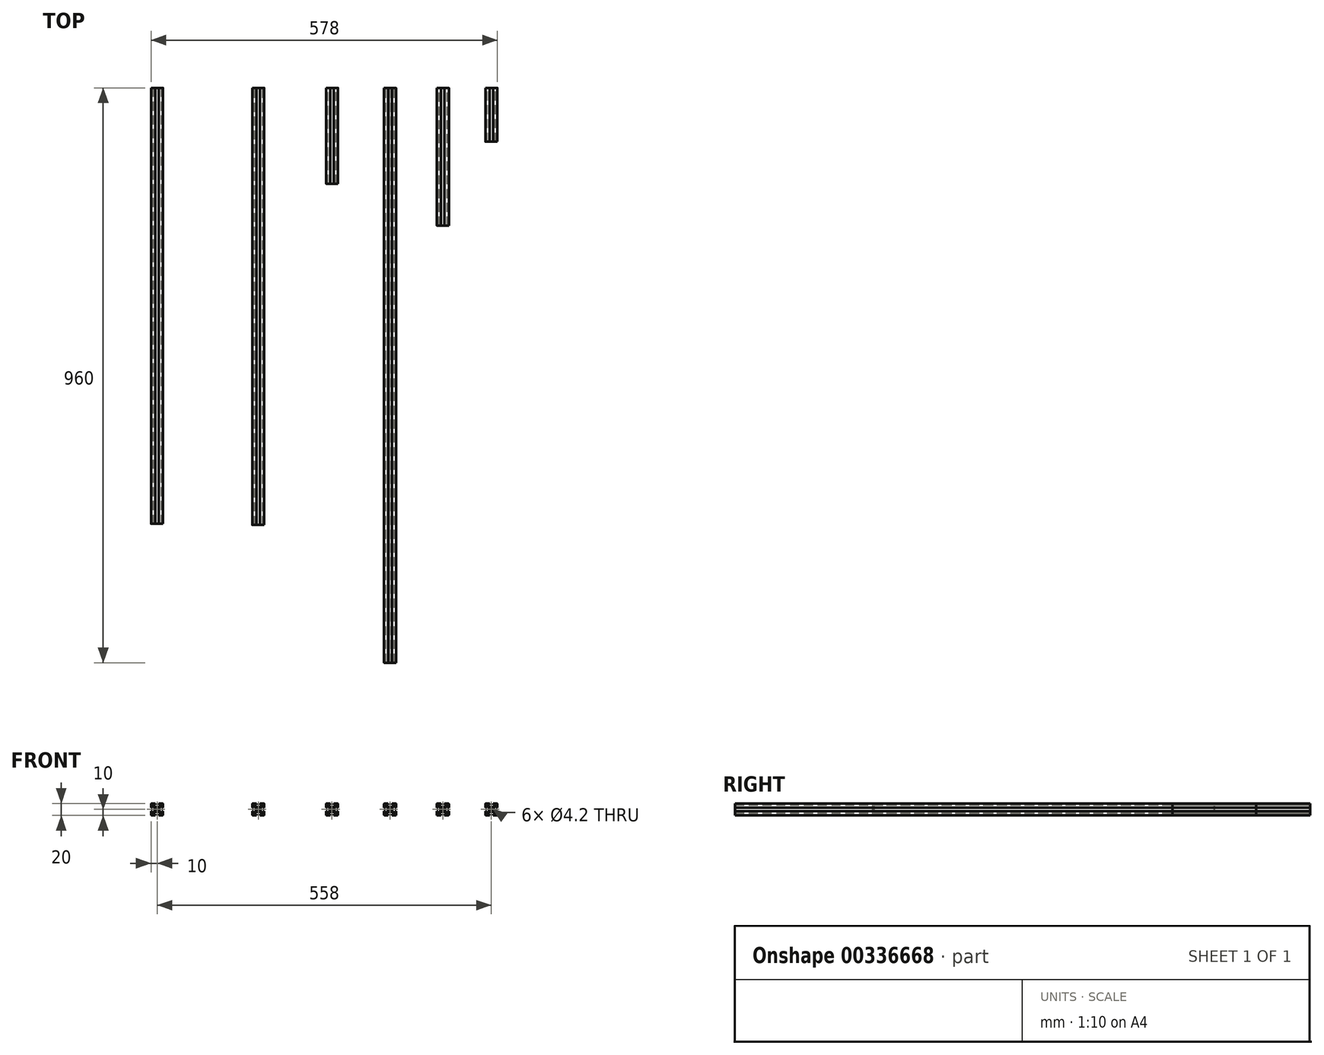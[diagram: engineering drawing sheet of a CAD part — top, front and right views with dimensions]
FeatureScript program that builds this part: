
annotation { "Feature Type Name" : "Feature", "Feature Type Description" : "" }
export const myFeature = defineFeature(function(context is Context, id is Id, definition is map)
    precondition{}
    {
        {
            var Q0;
            Q0=qCreatedBy(makeId("Front.planeOp"),FACE);
            var sketch = newSketch(context, id + "F0", { "sketchPlane" : qUnion([Q0])});
            skCircle(sketch, "E0", {"center": v(0, 0) * mm, "radius": 2.1 * mm});
            skLineSegment(sketch, "E1.bottom", {"start": v(9, 10) * mm, "end": v(3, 10) * mm});
            skLineSegment(sketch, "E1.top", {"start": v(9, -10) * mm, "end": v(3, -10) * mm});
            skLineSegment(sketch, "E1.left", {"start": v(10, 9) * mm, "end": v(10, 3) * mm});
            skLineSegment(sketch, "E1.right", {"start": v(-10, 9) * mm, "end": v(-10, 3) * mm});
            skLineSegment(sketch, "E2.bottom", {"start": v(2.94, 4) * mm, "end": v(-2.94, 4) * mm});
            skLineSegment(sketch, "E2.top", {"start": v(2.94, -4) * mm, "end": v(-2.94, -4) * mm});
            skLineSegment(sketch, "E2.left", {"start": v(4, 2.94) * mm, "end": v(4, -2.94) * mm});
            skLineSegment(sketch, "E2.right", {"start": v(-4, 2.94) * mm, "end": v(-4, -2.94) * mm});
            skLineSegment(sketch, "E3.bottom", {"start": v(6.94, 8) * mm, "end": v(3, 8) * mm});
            skLineSegment(sketch, "E3.top", {"start": v(6.94, -8) * mm, "end": v(3, -8) * mm});
            skLineSegment(sketch, "E3.left", {"start": v(8, 6.94) * mm, "end": v(8, 3) * mm});
            skLineSegment(sketch, "E3.right", {"start": v(-8, 6.94) * mm, "end": v(-8, 3) * mm});
            skLineSegment(sketch, "E4", {"start": v(-3, -10) * mm, "end": v(-3, -8) * mm});
            skLineSegment(sketch, "E5.MirrorCS", {"start": v(3, -10) * mm, "end": v(3, -8) * mm});
            skLineSegment(sketch, "E6.MirrorCS", {"start": v(-3, 10) * mm, "end": v(-3, 8) * mm});
            skLineSegment(sketch, "E7.MirrorCS", {"start": v(3, 10) * mm, "end": v(3, 8) * mm});
            skLineSegment(sketch, "E8", {"start": v(-10, 3) * mm, "end": v(-8, 3) * mm});
            skLineSegment(sketch, "E9.MirrorCS", {"start": v(-10, -3) * mm, "end": v(-8, -3) * mm});
            skLineSegment(sketch, "E10", {"start": v(8, 3) * mm, "end": v(10, 3) * mm});
            skLineSegment(sketch, "E11.MirrorCS", {"start": v(8, -3) * mm, "end": v(10, -3) * mm});
            skPoint(sketch, "E12", {"position": v(-8, -6.94) * mm});
            skPoint(sketch, "E13", {"position": v(6.94, 8) * mm});
            skPoint(sketch, "E14", {"position": v(-4, -2.94) * mm});
            skPoint(sketch, "E15", {"position": v(2.94, 4) * mm});
            skLineSegment(sketch, "E16", {"start": v(-8, -6.94) * mm, "end": v(-4, -2.94) * mm});
            skLineSegment(sketch, "E17", {"start": v(2.94, 4) * mm, "end": v(6.94, 8) * mm});
            skLineSegment(sketch, "E18.MirrorCS", {"start": v(-6.94, -8) * mm, "end": v(-2.94, -4) * mm});
            skLineSegment(sketch, "E19.1.0", {"start": v(6.94, -8) * mm, "end": v(2.94, -4) * mm});
            skLineSegment(sketch, "E19.2.0", {"start": v(8, 6.94) * mm, "end": v(4, 2.94) * mm});
            skLineSegment(sketch, "E19.3.0", {"start": v(-6.94, 8) * mm, "end": v(-2.94, 4) * mm});
            skLineSegment(sketch, "E20.1.0", {"start": v(8, -6.94) * mm, "end": v(4, -2.94) * mm});
            skLineSegment(sketch, "E20.2.0", {"start": v(6.94, 8) * mm, "end": v(2.94, 4) * mm});
            skLineSegment(sketch, "E20.3.0", {"start": v(-8, 6.94) * mm, "end": v(-4, 2.94) * mm});
            skLineSegment(sketch, "E21.trimOffspring", {"start": v(-3, 8) * mm, "end": v(-6.94, 8) * mm});
            skLineSegment(sketch, "E22.trimOffspring", {"start": v(-3, 10) * mm, "end": v(-9, 10) * mm});
            skLineSegment(sketch, "E23.trimOffspring", {"start": v(8, -3) * mm, "end": v(8, -6.94) * mm});
            skLineSegment(sketch, "E24.trimOffspring", {"start": v(10, -3) * mm, "end": v(10, -9) * mm});
            skLineSegment(sketch, "E25.trimOffspring", {"start": v(-3, -10) * mm, "end": v(-9, -10) * mm});
            skLineSegment(sketch, "E26.trimOffspring", {"start": v(-3, -8) * mm, "end": v(-6.94, -8) * mm});
            skLineSegment(sketch, "E27.trimOffspring", {"start": v(-10, -3) * mm, "end": v(-10, -9) * mm});
            skLineSegment(sketch, "E28.trimOffspring", {"start": v(-8, -3) * mm, "end": v(-8, -6.94) * mm});
            skArc(sketch, "E29.filletArc", {"start": v(-10, -9) * mm, "mid": v(-9.7, -9.7) * mm, "end": v(-9, -10) * mm});
            skArc(sketch, "E30.filletArc", {"start": v(9, -10) * mm, "mid": v(9.7, -9.7) * mm, "end": v(10, -9) * mm});
            skArc(sketch, "E31.filletArc", {"start": v(10, 9) * mm, "mid": v(9.7, 9.7) * mm, "end": v(9, 10) * mm});
            skArc(sketch, "E32.filletArc", {"start": v(-9, 10) * mm, "mid": v(-9.7, 9.7) * mm, "end": v(-10, 9) * mm});
            skSolve(sketch);
        }
        {
            var Q0;
            Q0=makeQuery(id+"F0.imprint","IMPRINT",FACE,{"disambiguationData":[TD([[makeQuery(id+"F0.imprint","IMPRINT",EDGE,{"derivedFrom":sQuery(id+"F0.wireOp",EDGE,"E0")}),-1.0]])]});
            extrude(context, id + "F1", {"entities" : qUnion([Q0]), "depth" : 960 * mm});
        }
        {
            var Q0;
            Q0 = qSketchRegion(id + "F0", true);
            extrude(context, id + "F2", {"entities" : qUnion([Q0]), "depth" : 230 * mm});
        }
        {
            var Q0;
            Q0=makeQuery(id+"F2.opExtrude","SWEPT_BODY",BODY,{"disambiguationData":[OSD([sQuery(id+"F0.wireOp",EDGE,"E0"),sQuery(id+"F0.wireOp",EDGE,"E1.bottom"),sQuery(id+"F0.wireOp",EDGE,"E1.top"),sQuery(id+"F0.wireOp",EDGE,"E1.left"),sQuery(id+"F0.wireOp",EDGE,"E1.right"),sQuery(id+"F0.wireOp",EDGE,"E2.bottom"),sQuery(id+"F0.wireOp",EDGE,"E2.top"),sQuery(id+"F0.wireOp",EDGE,"E2.left"),sQuery(id+"F0.wireOp",EDGE,"E2.right"),sQuery(id+"F0.wireOp",EDGE,"E3.bottom"),sQuery(id+"F0.wireOp",EDGE,"E3.top"),sQuery(id+"F0.wireOp",EDGE,"E3.left"),sQuery(id+"F0.wireOp",EDGE,"E3.right"),sQuery(id+"F0.wireOp",EDGE,"E4"),sQuery(id+"F0.wireOp",EDGE,"E5.MirrorCS"),sQuery(id+"F0.wireOp",EDGE,"E6.MirrorCS"),sQuery(id+"F0.wireOp",EDGE,"E7.MirrorCS"),sQuery(id+"F0.wireOp",EDGE,"E8"),sQuery(id+"F0.wireOp",EDGE,"E9.MirrorCS"),sQuery(id+"F0.wireOp",EDGE,"E10"),sQuery(id+"F0.wireOp",EDGE,"E11.MirrorCS"),sQuery(id+"F0.wireOp",EDGE,"E16"),sQuery(id+"F0.wireOp",EDGE,"E18.MirrorCS"),sQuery(id+"F0.wireOp",EDGE,"E19.1.0"),sQuery(id+"F0.wireOp",EDGE,"E19.2.0"),sQuery(id+"F0.wireOp",EDGE,"E19.3.0"),sQuery(id+"F0.wireOp",EDGE,"E20.1.0"),sQuery(id+"F0.wireOp",EDGE,"E20.2.0"),sQuery(id+"F0.wireOp",EDGE,"E20.3.0"),sQuery(id+"F0.wireOp",EDGE,"E21.trimOffspring"),sQuery(id+"F0.wireOp",EDGE,"E22.trimOffspring"),sQuery(id+"F0.wireOp",EDGE,"E23.trimOffspring"),sQuery(id+"F0.wireOp",EDGE,"E24.trimOffspring"),sQuery(id+"F0.wireOp",EDGE,"E25.trimOffspring"),sQuery(id+"F0.wireOp",EDGE,"E26.trimOffspring"),sQuery(id+"F0.wireOp",EDGE,"E27.trimOffspring"),sQuery(id+"F0.wireOp",EDGE,"E28.trimOffspring"),sQuery(id+"F0.wireOp",EDGE,"E29.filletArc"),sQuery(id+"F0.wireOp",EDGE,"E30.filletArc"),sQuery(id+"F0.wireOp",EDGE,"E31.filletArc"),sQuery(id+"F0.wireOp",EDGE,"E32.filletArc")])]});
            transform(context, id + "F3", {"entities" : qUnion([Q0]), "transformType" : TransformType.TRANSLATION_3D, "dx" : 88 * mm, "dy" : 0 * mm, "dz" : 0 * mm, "makeCopy" : false});
        }
        {
            var Q0;
            Q0 = qSketchRegion(id + "F0", true);
            extrude(context, id + "F4", {"entities" : qUnion([Q0]), "depth" : 160 * mm});
        }
        {
            var Q0;
            Q0 = qSketchRegion(id + "F0", true);
            extrude(context, id + "F5", {"entities" : qUnion([Q0]), "depth" : 90 * mm});
        }
        {
            var Q0;
            Q0=makeQuery(id+"F5.opExtrude","SWEPT_BODY",BODY,{"disambiguationData":[OSD([sQuery(id+"F0.wireOp",EDGE,"E0"),sQuery(id+"F0.wireOp",EDGE,"E1.bottom"),sQuery(id+"F0.wireOp",EDGE,"E1.top"),sQuery(id+"F0.wireOp",EDGE,"E1.left"),sQuery(id+"F0.wireOp",EDGE,"E1.right"),sQuery(id+"F0.wireOp",EDGE,"E2.bottom"),sQuery(id+"F0.wireOp",EDGE,"E2.top"),sQuery(id+"F0.wireOp",EDGE,"E2.left"),sQuery(id+"F0.wireOp",EDGE,"E2.right"),sQuery(id+"F0.wireOp",EDGE,"E3.bottom"),sQuery(id+"F0.wireOp",EDGE,"E3.top"),sQuery(id+"F0.wireOp",EDGE,"E3.left"),sQuery(id+"F0.wireOp",EDGE,"E3.right"),sQuery(id+"F0.wireOp",EDGE,"E4"),sQuery(id+"F0.wireOp",EDGE,"E5.MirrorCS"),sQuery(id+"F0.wireOp",EDGE,"E6.MirrorCS"),sQuery(id+"F0.wireOp",EDGE,"E7.MirrorCS"),sQuery(id+"F0.wireOp",EDGE,"E8"),sQuery(id+"F0.wireOp",EDGE,"E9.MirrorCS"),sQuery(id+"F0.wireOp",EDGE,"E10"),sQuery(id+"F0.wireOp",EDGE,"E11.MirrorCS"),sQuery(id+"F0.wireOp",EDGE,"E16"),sQuery(id+"F0.wireOp",EDGE,"E18.MirrorCS"),sQuery(id+"F0.wireOp",EDGE,"E19.1.0"),sQuery(id+"F0.wireOp",EDGE,"E19.2.0"),sQuery(id+"F0.wireOp",EDGE,"E19.3.0"),sQuery(id+"F0.wireOp",EDGE,"E20.1.0"),sQuery(id+"F0.wireOp",EDGE,"E20.2.0"),sQuery(id+"F0.wireOp",EDGE,"E20.3.0"),sQuery(id+"F0.wireOp",EDGE,"E21.trimOffspring"),sQuery(id+"F0.wireOp",EDGE,"E22.trimOffspring"),sQuery(id+"F0.wireOp",EDGE,"E23.trimOffspring"),sQuery(id+"F0.wireOp",EDGE,"E24.trimOffspring"),sQuery(id+"F0.wireOp",EDGE,"E25.trimOffspring"),sQuery(id+"F0.wireOp",EDGE,"E26.trimOffspring"),sQuery(id+"F0.wireOp",EDGE,"E27.trimOffspring"),sQuery(id+"F0.wireOp",EDGE,"E28.trimOffspring"),sQuery(id+"F0.wireOp",EDGE,"E29.filletArc"),sQuery(id+"F0.wireOp",EDGE,"E30.filletArc"),sQuery(id+"F0.wireOp",EDGE,"E31.filletArc"),sQuery(id+"F0.wireOp",EDGE,"E32.filletArc")])]});
            transform(context, id + "F6", {"entities" : qUnion([Q0]), "transformType" : TransformType.TRANSLATION_3D, "dx" : 169 * mm, "dy" : 0 * mm, "dz" : 0 * mm, "makeCopy" : false});
        }
        {
            var Q0;
            Q0=makeQuery(id+"F4.opExtrude","SWEPT_BODY",BODY,{"disambiguationData":[OSD([sQuery(id+"F0.wireOp",EDGE,"E0"),sQuery(id+"F0.wireOp",EDGE,"E1.bottom"),sQuery(id+"F0.wireOp",EDGE,"E1.top"),sQuery(id+"F0.wireOp",EDGE,"E1.left"),sQuery(id+"F0.wireOp",EDGE,"E1.right"),sQuery(id+"F0.wireOp",EDGE,"E2.bottom"),sQuery(id+"F0.wireOp",EDGE,"E2.top"),sQuery(id+"F0.wireOp",EDGE,"E2.left"),sQuery(id+"F0.wireOp",EDGE,"E2.right"),sQuery(id+"F0.wireOp",EDGE,"E3.bottom"),sQuery(id+"F0.wireOp",EDGE,"E3.top"),sQuery(id+"F0.wireOp",EDGE,"E3.left"),sQuery(id+"F0.wireOp",EDGE,"E3.right"),sQuery(id+"F0.wireOp",EDGE,"E4"),sQuery(id+"F0.wireOp",EDGE,"E5.MirrorCS"),sQuery(id+"F0.wireOp",EDGE,"E6.MirrorCS"),sQuery(id+"F0.wireOp",EDGE,"E7.MirrorCS"),sQuery(id+"F0.wireOp",EDGE,"E8"),sQuery(id+"F0.wireOp",EDGE,"E9.MirrorCS"),sQuery(id+"F0.wireOp",EDGE,"E10"),sQuery(id+"F0.wireOp",EDGE,"E11.MirrorCS"),sQuery(id+"F0.wireOp",EDGE,"E16"),sQuery(id+"F0.wireOp",EDGE,"E18.MirrorCS"),sQuery(id+"F0.wireOp",EDGE,"E19.1.0"),sQuery(id+"F0.wireOp",EDGE,"E19.2.0"),sQuery(id+"F0.wireOp",EDGE,"E19.3.0"),sQuery(id+"F0.wireOp",EDGE,"E20.1.0"),sQuery(id+"F0.wireOp",EDGE,"E20.2.0"),sQuery(id+"F0.wireOp",EDGE,"E20.3.0"),sQuery(id+"F0.wireOp",EDGE,"E21.trimOffspring"),sQuery(id+"F0.wireOp",EDGE,"E22.trimOffspring"),sQuery(id+"F0.wireOp",EDGE,"E23.trimOffspring"),sQuery(id+"F0.wireOp",EDGE,"E24.trimOffspring"),sQuery(id+"F0.wireOp",EDGE,"E25.trimOffspring"),sQuery(id+"F0.wireOp",EDGE,"E26.trimOffspring"),sQuery(id+"F0.wireOp",EDGE,"E27.trimOffspring"),sQuery(id+"F0.wireOp",EDGE,"E28.trimOffspring"),sQuery(id+"F0.wireOp",EDGE,"E29.filletArc"),sQuery(id+"F0.wireOp",EDGE,"E30.filletArc"),sQuery(id+"F0.wireOp",EDGE,"E31.filletArc"),sQuery(id+"F0.wireOp",EDGE,"E32.filletArc")])]});
            transform(context, id + "F7", {"entities" : qUnion([Q0]), "transformType" : TransformType.TRANSLATION_3D, "dx" : -97 * mm, "dy" : 0 * mm, "dz" : 0 * mm, "makeCopy" : false});
        }
        {
            var Q0;
            Q0 = qSketchRegion(id + "F0", true);
            extrude(context, id + "F8", {"entities" : qUnion([Q0]), "depth" : 730 * mm});
        }
        {
            var Q0;
            Q0=makeQuery(id+"F8.opExtrude","SWEPT_BODY",BODY,{"disambiguationData":[OSD([sQuery(id+"F0.wireOp",EDGE,"E0"),sQuery(id+"F0.wireOp",EDGE,"E1.bottom"),sQuery(id+"F0.wireOp",EDGE,"E1.top"),sQuery(id+"F0.wireOp",EDGE,"E1.left"),sQuery(id+"F0.wireOp",EDGE,"E1.right"),sQuery(id+"F0.wireOp",EDGE,"E2.bottom"),sQuery(id+"F0.wireOp",EDGE,"E2.top"),sQuery(id+"F0.wireOp",EDGE,"E2.left"),sQuery(id+"F0.wireOp",EDGE,"E2.right"),sQuery(id+"F0.wireOp",EDGE,"E3.bottom"),sQuery(id+"F0.wireOp",EDGE,"E3.top"),sQuery(id+"F0.wireOp",EDGE,"E3.left"),sQuery(id+"F0.wireOp",EDGE,"E3.right"),sQuery(id+"F0.wireOp",EDGE,"E4"),sQuery(id+"F0.wireOp",EDGE,"E5.MirrorCS"),sQuery(id+"F0.wireOp",EDGE,"E6.MirrorCS"),sQuery(id+"F0.wireOp",EDGE,"E7.MirrorCS"),sQuery(id+"F0.wireOp",EDGE,"E8"),sQuery(id+"F0.wireOp",EDGE,"E9.MirrorCS"),sQuery(id+"F0.wireOp",EDGE,"E10"),sQuery(id+"F0.wireOp",EDGE,"E11.MirrorCS"),sQuery(id+"F0.wireOp",EDGE,"E16"),sQuery(id+"F0.wireOp",EDGE,"E18.MirrorCS"),sQuery(id+"F0.wireOp",EDGE,"E19.1.0"),sQuery(id+"F0.wireOp",EDGE,"E19.2.0"),sQuery(id+"F0.wireOp",EDGE,"E19.3.0"),sQuery(id+"F0.wireOp",EDGE,"E20.1.0"),sQuery(id+"F0.wireOp",EDGE,"E20.2.0"),sQuery(id+"F0.wireOp",EDGE,"E20.3.0"),sQuery(id+"F0.wireOp",EDGE,"E21.trimOffspring"),sQuery(id+"F0.wireOp",EDGE,"E22.trimOffspring"),sQuery(id+"F0.wireOp",EDGE,"E23.trimOffspring"),sQuery(id+"F0.wireOp",EDGE,"E24.trimOffspring"),sQuery(id+"F0.wireOp",EDGE,"E25.trimOffspring"),sQuery(id+"F0.wireOp",EDGE,"E26.trimOffspring"),sQuery(id+"F0.wireOp",EDGE,"E27.trimOffspring"),sQuery(id+"F0.wireOp",EDGE,"E28.trimOffspring"),sQuery(id+"F0.wireOp",EDGE,"E29.filletArc"),sQuery(id+"F0.wireOp",EDGE,"E30.filletArc"),sQuery(id+"F0.wireOp",EDGE,"E31.filletArc"),sQuery(id+"F0.wireOp",EDGE,"E32.filletArc")])]});
            transform(context, id + "F9", {"entities" : qUnion([Q0]), "transformType" : TransformType.TRANSLATION_3D, "dx" : -220 * mm, "dy" : 0 * mm, "dz" : 0 * mm, "makeCopy" : false});
        }
        {
            var Q0;
            Q0 = qSketchRegion(id + "F0", true);
            extrude(context, id + "F10", {"entities" : qUnion([Q0]), "depth" : 728 * mm});
        }
        {
            var Q0;
            Q0=makeQuery(id+"F10.opExtrude","SWEPT_BODY",BODY,{"disambiguationData":[OSD([sQuery(id+"F0.wireOp",EDGE,"E0"),sQuery(id+"F0.wireOp",EDGE,"E1.bottom"),sQuery(id+"F0.wireOp",EDGE,"E1.top"),sQuery(id+"F0.wireOp",EDGE,"E1.left"),sQuery(id+"F0.wireOp",EDGE,"E1.right"),sQuery(id+"F0.wireOp",EDGE,"E2.bottom"),sQuery(id+"F0.wireOp",EDGE,"E2.top"),sQuery(id+"F0.wireOp",EDGE,"E2.left"),sQuery(id+"F0.wireOp",EDGE,"E2.right"),sQuery(id+"F0.wireOp",EDGE,"E3.bottom"),sQuery(id+"F0.wireOp",EDGE,"E3.top"),sQuery(id+"F0.wireOp",EDGE,"E3.left"),sQuery(id+"F0.wireOp",EDGE,"E3.right"),sQuery(id+"F0.wireOp",EDGE,"E4"),sQuery(id+"F0.wireOp",EDGE,"E5.MirrorCS"),sQuery(id+"F0.wireOp",EDGE,"E6.MirrorCS"),sQuery(id+"F0.wireOp",EDGE,"E7.MirrorCS"),sQuery(id+"F0.wireOp",EDGE,"E8"),sQuery(id+"F0.wireOp",EDGE,"E9.MirrorCS"),sQuery(id+"F0.wireOp",EDGE,"E10"),sQuery(id+"F0.wireOp",EDGE,"E11.MirrorCS"),sQuery(id+"F0.wireOp",EDGE,"E16"),sQuery(id+"F0.wireOp",EDGE,"E18.MirrorCS"),sQuery(id+"F0.wireOp",EDGE,"E19.1.0"),sQuery(id+"F0.wireOp",EDGE,"E19.2.0"),sQuery(id+"F0.wireOp",EDGE,"E19.3.0"),sQuery(id+"F0.wireOp",EDGE,"E20.1.0"),sQuery(id+"F0.wireOp",EDGE,"E20.2.0"),sQuery(id+"F0.wireOp",EDGE,"E20.3.0"),sQuery(id+"F0.wireOp",EDGE,"E21.trimOffspring"),sQuery(id+"F0.wireOp",EDGE,"E22.trimOffspring"),sQuery(id+"F0.wireOp",EDGE,"E23.trimOffspring"),sQuery(id+"F0.wireOp",EDGE,"E24.trimOffspring"),sQuery(id+"F0.wireOp",EDGE,"E25.trimOffspring"),sQuery(id+"F0.wireOp",EDGE,"E26.trimOffspring"),sQuery(id+"F0.wireOp",EDGE,"E27.trimOffspring"),sQuery(id+"F0.wireOp",EDGE,"E28.trimOffspring"),sQuery(id+"F0.wireOp",EDGE,"E29.filletArc"),sQuery(id+"F0.wireOp",EDGE,"E30.filletArc"),sQuery(id+"F0.wireOp",EDGE,"E31.filletArc"),sQuery(id+"F0.wireOp",EDGE,"E32.filletArc")])]});
            transform(context, id + "F11", {"entities" : qUnion([Q0]), "transformType" : TransformType.TRANSLATION_3D, "dx" : -389 * mm, "dy" : 0 * mm, "dz" : 0 * mm, "makeCopy" : false});
        }
    });
